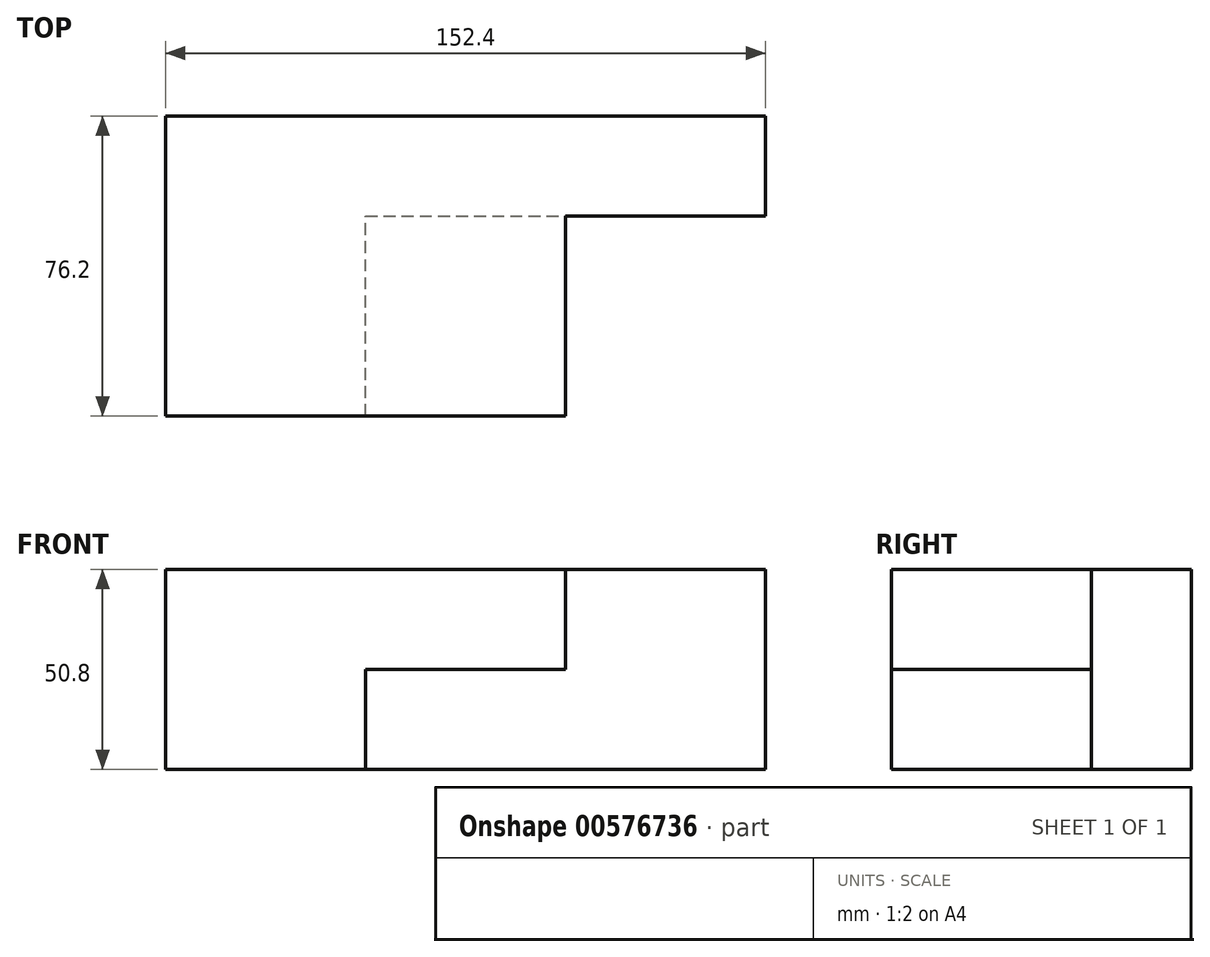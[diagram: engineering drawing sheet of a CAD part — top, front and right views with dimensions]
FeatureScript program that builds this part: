
annotation { "Feature Type Name" : "Feature", "Feature Type Description" : "" }
export const myFeature = defineFeature(function(context is Context, id is Id, definition is map)
    precondition{}
    {
        {
            var Q0;
            Q0=qCreatedBy(makeId("Front.planeOp"),FACE);
            var sketch = newSketch(context, id + "F0", { "sketchPlane" : qUnion([Q0])});
            skLineSegment(sketch, "E0.bottom", {"start": v(-79.9, -2.65) * mm, "end": v(72.5, -2.65) * mm});
            skLineSegment(sketch, "E0.top", {"start": v(-79.9, -53.45) * mm, "end": v(72.5, -53.45) * mm});
            skLineSegment(sketch, "E0.left", {"start": v(-79.9, -2.65) * mm, "end": v(-79.9, -53.45) * mm});
            skLineSegment(sketch, "E0.right", {"start": v(72.5, -2.65) * mm, "end": v(72.5, -53.45) * mm});
            skLineSegment(sketch, "E1", {"start": v(-29.1, -53.45) * mm, "end": v(-29.1, -28.05) * mm});
            skLineSegment(sketch, "E2", {"start": v(-29.1, -28.05) * mm, "end": v(21.7, -28.05) * mm});
            skLineSegment(sketch, "E3", {"start": v(21.7, -28.05) * mm, "end": v(21.7, -2.65) * mm});
            skSolve(sketch);
        }
        {
            var Q0;
            {var subQ1=sQuery(id+"F0.wireOp",EDGE,"E0.left");Q0=makeQuery(id+"F0.imprint","IMPRINT",FACE,{"disambiguationData":[TD([[makeQuery(id+"F0.imprint","IMPRINT",EDGE,{"derivedFrom":subQ1}),1.0]])]});}
            extrude(context, id + "F1", {"entities" : qUnion([Q0]), "depth" : 76.2 * mm, "offsetDistance" : 25.4 * mm});
        }
        {
            var Q0;
            {var subQ0=sQuery(id+"F0.wireOp",EDGE,"E0.right");Q0=makeQuery(id+"F0.imprint","IMPRINT",FACE,{"disambiguationData":[TD([[makeQuery(id+"F0.imprint","IMPRINT",EDGE,{"derivedFrom":subQ0}),-1.0]])]});}
            extrude(context, id + "F2", {"entities" : qUnion([Q0]), "operationType" : NewBodyOperationType.ADD, "depth" : 25.4 * mm, "offsetDistance" : 25.4 * mm});
        }
    });
